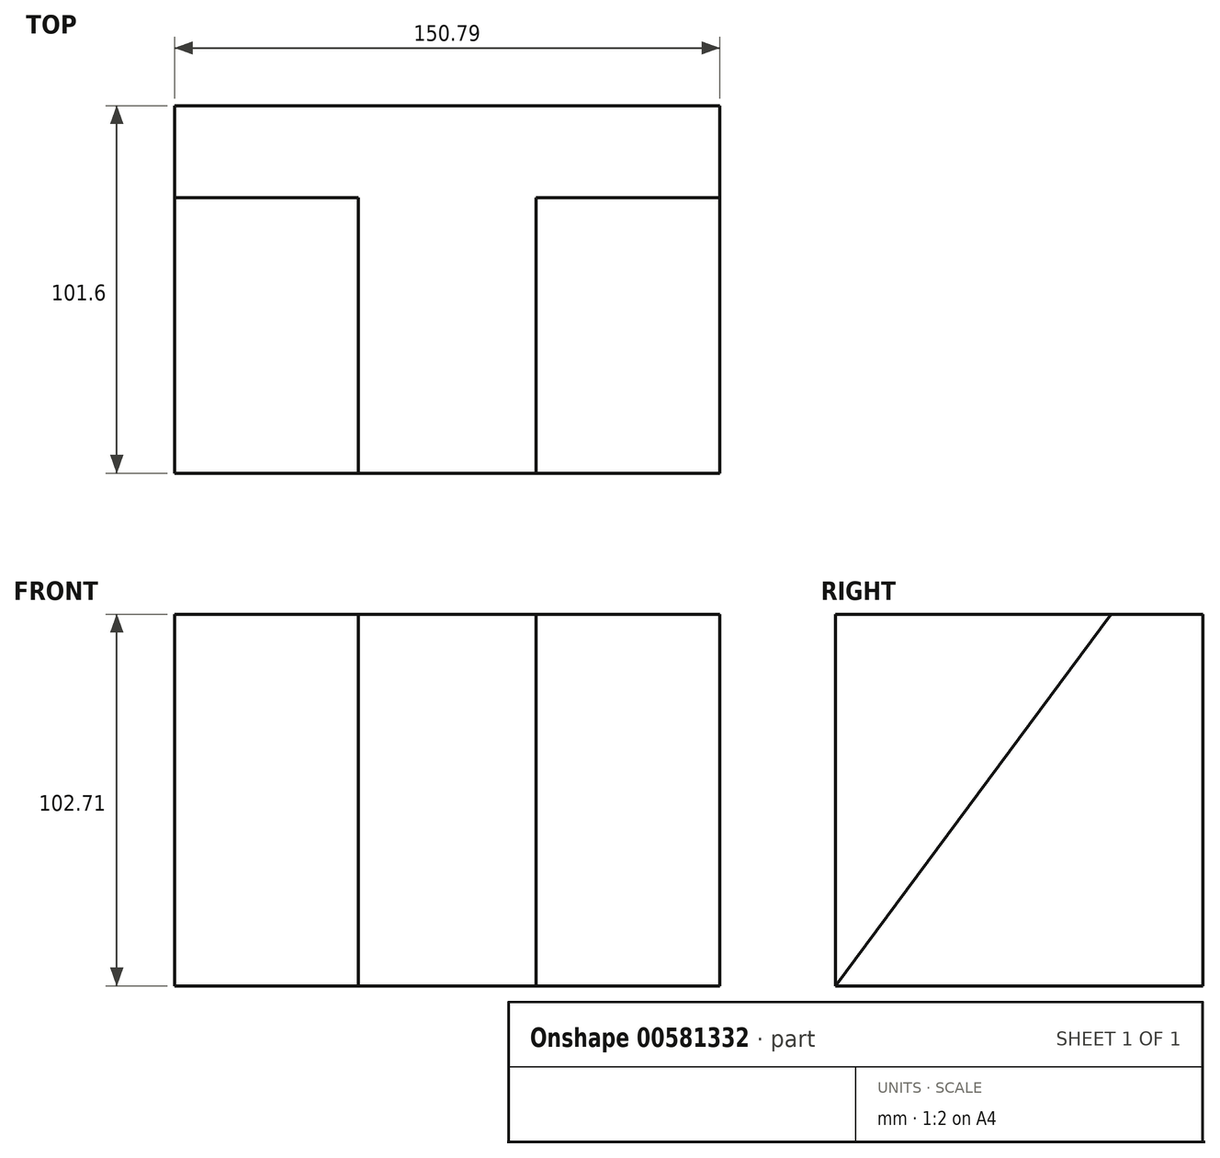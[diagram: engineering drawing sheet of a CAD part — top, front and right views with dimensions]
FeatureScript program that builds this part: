
annotation { "Feature Type Name" : "Feature", "Feature Type Description" : "" }
export const myFeature = defineFeature(function(context is Context, id is Id, definition is map)
    precondition{}
    {
        {
            var Q0;
            Q0=qCreatedBy(makeId("Front.planeOp"),FACE);
            var sketch = newSketch(context, id + "F0", { "sketchPlane" : qUnion([Q0])});
            skLineSegment(sketch, "E0.bottom", {"start": v(-75.88, 56.1) * mm, "end": v(74.91, 56.1) * mm});
            skLineSegment(sketch, "E0.top", {"start": v(-75.88, -46.62) * mm, "end": v(74.91, -46.62) * mm});
            skLineSegment(sketch, "E0.left", {"start": v(-75.88, 56.1) * mm, "end": v(-75.88, -46.62) * mm});
            skLineSegment(sketch, "E0.right", {"start": v(74.91, 56.1) * mm, "end": v(74.91, -46.62) * mm});
            skSolve(sketch);
        }
        {
            var Q0;
            Q0=makeQuery(id+"F0.imprint","IMPRINT",FACE,{"disambiguationData":[TD([[makeQuery(id+"F0.imprint","IMPRINT",EDGE,{"derivedFrom":sQuery(id+"F0.wireOp",EDGE,"E0.bottom")}),-1.0]])]});
            extrude(context, id + "F1", {"entities" : qUnion([Q0]), "depth" : 76.2 * mm, "offsetDistance" : 25.4 * mm});
        }
        {
            var Q0;
            Q0=makeQuery(id+"F1.opExtrude","SWEPT_FACE",FACE,{"disambiguationData":[OSD([sQuery(id+"F0.wireOp",EDGE,"E0.right")])]});
            var sketch = newSketch(context, id + "F2", { "sketchPlane" : qUnion([Q0])});
            skLineSegment(sketch, "E1", {"start": v(-76.2, -46.62) * mm, "end": v(0, 56.1) * mm});
            skSolve(sketch);
        }
        {
            var Q0;
            Q0=makeQuery(id+"F2.imprint","IMPRINT",FACE,{"disambiguationData":[TD([[makeQuery(id+"F2.imprint","IMPRINT",EDGE,{"derivedFrom":sQuery(id+"F2.wireOp",EDGE,"E1")}),1.0]])]});
            extrude(context, id + "F3", {"entities" : qUnion([Q0]), "operationType" : NewBodyOperationType.REMOVE, "oppositeDirection" : true, "depth" : 50.8 * mm, "offsetDistance" : 25.4 * mm});
        }
        {
            var Q0;
            Q0=makeQuery(id+"F1.opExtrude","SWEPT_FACE",FACE,{"disambiguationData":[OSD([sQuery(id+"F0.wireOp",EDGE,"E0.left")])]});
            var sketch = newSketch(context, id + "F4", { "sketchPlane" : qUnion([Q0])});
            skLineSegment(sketch, "E2", {"start": v(0, 56.1) * mm, "end": v(76.2, -46.62) * mm});
            skSolve(sketch);
        }
        {
            var Q0;
            Q0=makeQuery(id+"F4.imprint","IMPRINT",FACE,{"disambiguationData":[TD([[makeQuery(id+"F4.imprint","IMPRINT",EDGE,{"derivedFrom":sQuery(id+"F4.wireOp",EDGE,"E2")}),1.0]])]});
            extrude(context, id + "F5", {"entities" : qUnion([Q0]), "operationType" : NewBodyOperationType.REMOVE, "oppositeDirection" : true, "depth" : 50.8 * mm, "offsetDistance" : 25.4 * mm});
        }
        {
            var Q0;
            Q0=makeQuery(id+"F1.opExtrude","CAP_FACE",FACE,{"disambiguationData":[OSD([sQuery(id+"F0.wireOp",EDGE,"E0.bottom"),sQuery(id+"F0.wireOp",EDGE,"E0.top"),sQuery(id+"F0.wireOp",EDGE,"E0.left"),sQuery(id+"F0.wireOp",EDGE,"E0.right")])],"isStart":true});
            var sketch = newSketch(context, id + "F6", { "sketchPlane" : qUnion([Q0])});
            skLineSegment(sketch, "E3.bottom", {"start": v(-74.91, 56.1) * mm, "end": v(75.88, 56.1) * mm});
            skLineSegment(sketch, "E3.top", {"start": v(-74.91, -46.62) * mm, "end": v(75.88, -46.62) * mm});
            skLineSegment(sketch, "E3.left", {"start": v(-74.91, 56.1) * mm, "end": v(-74.91, -46.62) * mm});
            skLineSegment(sketch, "E3.right", {"start": v(75.88, 56.1) * mm, "end": v(75.88, -46.62) * mm});
            skSolve(sketch);
        }
        {
            var Q0;
            Q0=makeQuery(id+"F6.imprint","IMPRINT",FACE,{"disambiguationData":[TD([[makeQuery(id+"F6.imprint","IMPRINT",EDGE,{"derivedFrom":sQuery(id+"F6.wireOp",EDGE,"E3.top")}),-1.0]])]});
            extrude(context, id + "F7", {"entities" : qUnion([Q0]), "operationType" : NewBodyOperationType.ADD, "depth" : 25.4 * mm, "offsetDistance" : 25.4 * mm});
        }
    });
